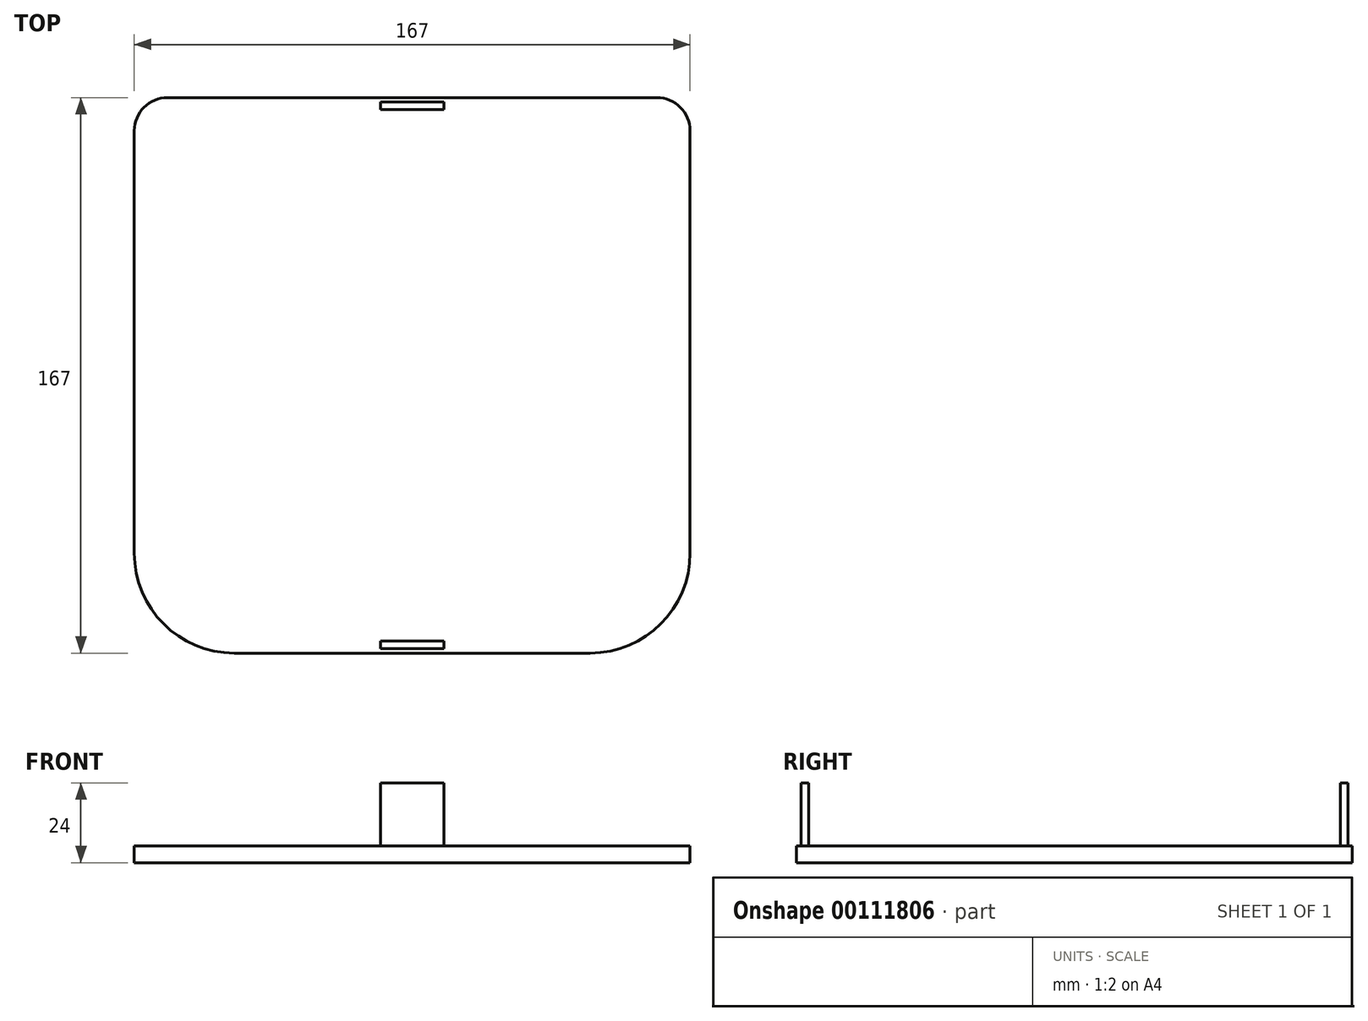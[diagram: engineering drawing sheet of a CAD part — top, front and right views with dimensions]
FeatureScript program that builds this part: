
annotation { "Feature Type Name" : "Feature", "Feature Type Description" : "" }
export const myFeature = defineFeature(function(context is Context, id is Id, definition is map)
    precondition{}
    {
        {
            var Q0;
            Q0=qCreatedBy(makeId("Top.planeOp"),FACE);
            var sketch = newSketch(context, id + "F0", { "sketchPlane" : qUnion([Q0])});
            skLineSegment(sketch, "E0.bottom", {"start": v(53.5, -83.5) * mm, "end": v(-53.5, -83.5) * mm});
            skLineSegment(sketch, "E0.top", {"start": v(73.5, 83.5) * mm, "end": v(-73.5, 83.5) * mm});
            skLineSegment(sketch, "E0.left", {"start": v(83.5, -53.5) * mm, "end": v(83.5, 73.5) * mm});
            skLineSegment(sketch, "E0.right", {"start": v(-83.5, -53.5) * mm, "end": v(-83.5, 73.5) * mm});
            skPoint(sketch, "E0.middle", {"position": v(0, 0) * mm});
            skPoint(sketch, "E1.visualSharp", {"position": v(-83.5, -83.5) * mm});
            skArc(sketch, "E1.filletArc", {"start": v(-83.5, -53.5) * mm, "mid": v(-74.71, -74.71) * mm, "end": v(-53.5, -83.5) * mm});
            skPoint(sketch, "E2.visualSharp", {"position": v(83.5, -83.5) * mm});
            skArc(sketch, "E2.filletArc", {"start": v(53.5, -83.5) * mm, "mid": v(74.71, -74.71) * mm, "end": v(83.5, -53.5) * mm});
            skPoint(sketch, "E3.visualSharp", {"position": v(-83.5, 83.5) * mm});
            skArc(sketch, "E3.filletArc", {"start": v(-73.5, 83.5) * mm, "mid": v(-80.57, 80.57) * mm, "end": v(-83.5, 73.5) * mm});
            skPoint(sketch, "E4.visualSharp", {"position": v(83.5, 83.5) * mm});
            skArc(sketch, "E4.filletArc", {"start": v(83.5, 73.5) * mm, "mid": v(80.57, 80.57) * mm, "end": v(73.5, 83.5) * mm});
            skSolve(sketch);
        }
        {
            var Q0;
            Q0=makeQuery(id+"F0.imprint","IMPRINT",FACE,{"disambiguationData":[TD([[makeQuery(id+"F0.imprint","IMPRINT",EDGE,{"derivedFrom":sQuery(id+"F0.wireOp",EDGE,"E0.bottom")}),-1.0]])]});
            extrude(context, id + "F1", {"entities" : qUnion([Q0]), "depth" : 5 * mm});
        }
        {
            var Q0;
            Q0=makeQuery(id+"F1.opExtrude","CAP_FACE",FACE,{"disambiguationData":[OSD([sQuery(id+"F0.wireOp",EDGE,"E0.bottom"),sQuery(id+"F0.wireOp",EDGE,"E0.top"),sQuery(id+"F0.wireOp",EDGE,"E0.left"),sQuery(id+"F0.wireOp",EDGE,"E0.right"),sQuery(id+"F0.wireOp",EDGE,"E1.filletArc"),sQuery(id+"F0.wireOp",EDGE,"E2.filletArc"),sQuery(id+"F0.wireOp",EDGE,"E3.filletArc"),sQuery(id+"F0.wireOp",EDGE,"E4.filletArc")])],"isStart":false});
            var sketch = newSketch(context, id + "F2", { "sketchPlane" : qUnion([Q0])});
            skLineSegment(sketch, "E5.bottom", {"start": v(9.5, -82.12) * mm, "end": v(-9.5, -82.12) * mm});
            skLineSegment(sketch, "E5.top", {"start": v(9.5, -79.87) * mm, "end": v(-9.5, -79.87) * mm});
            skLineSegment(sketch, "E5.left", {"start": v(9.5, -82.12) * mm, "end": v(9.5, -79.87) * mm});
            skLineSegment(sketch, "E5.right", {"start": v(-9.5, -82.12) * mm, "end": v(-9.5, -79.87) * mm});
            skPoint(sketch, "E5.middle", {"position": v(0, -81) * mm});
            skSolve(sketch);
        }
        {
            var Q0;
            Q0 = qSketchRegion(id + "F2", true);
            extrude(context, id + "F3", {"entities" : qUnion([Q0]), "operationType" : NewBodyOperationType.ADD, "depth" : 19 * mm});
        }
        {
            var Q0;
            Q0=makeQuery(id+"F1.opExtrude","CAP_FACE",FACE,{"disambiguationData":[OSD([sQuery(id+"F0.wireOp",EDGE,"E0.bottom"),sQuery(id+"F0.wireOp",EDGE,"E0.top"),sQuery(id+"F0.wireOp",EDGE,"E0.left"),sQuery(id+"F0.wireOp",EDGE,"E0.right"),sQuery(id+"F0.wireOp",EDGE,"E1.filletArc"),sQuery(id+"F0.wireOp",EDGE,"E2.filletArc"),sQuery(id+"F0.wireOp",EDGE,"E3.filletArc"),sQuery(id+"F0.wireOp",EDGE,"E4.filletArc")])],"isStart":false});
            var sketch = newSketch(context, id + "F4", { "sketchPlane" : qUnion([Q0])});
            skLineSegment(sketch, "E6.bottom", {"start": v(9.5, 79.88) * mm, "end": v(-9.5, 79.88) * mm});
            skLineSegment(sketch, "E6.top", {"start": v(9.5, 82.12) * mm, "end": v(-9.5, 82.12) * mm});
            skLineSegment(sketch, "E6.left", {"start": v(9.5, 79.88) * mm, "end": v(9.5, 82.12) * mm});
            skLineSegment(sketch, "E6.right", {"start": v(-9.5, 79.88) * mm, "end": v(-9.5, 82.12) * mm});
            skPoint(sketch, "E6.middle", {"position": v(0, 81) * mm});
            skSolve(sketch);
        }
        {
            var Q0;
            Q0 = qSketchRegion(id + "F4", true);
            extrude(context, id + "F5", {"entities" : qUnion([Q0]), "operationType" : NewBodyOperationType.ADD, "depth" : 19 * mm});
        }
    });
